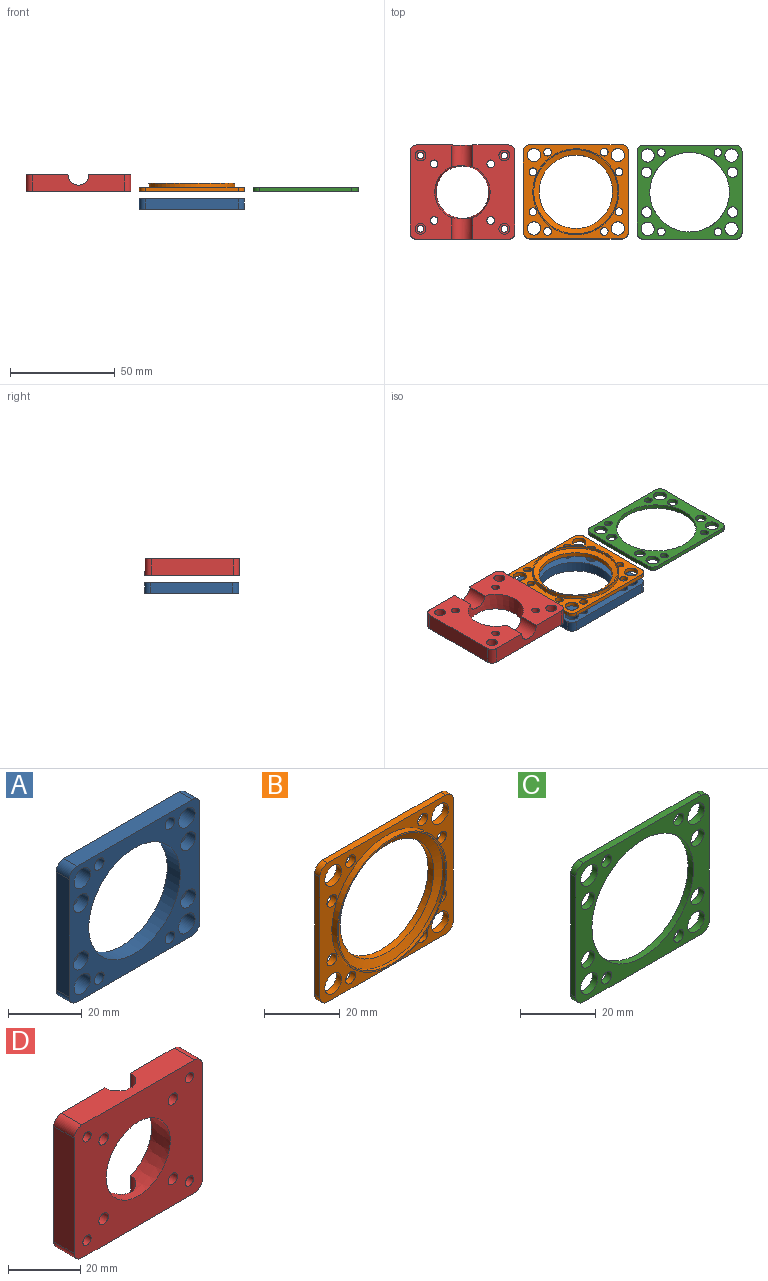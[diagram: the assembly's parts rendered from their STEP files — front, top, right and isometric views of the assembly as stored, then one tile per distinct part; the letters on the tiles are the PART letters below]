
ASSEMBLY  parts=4 mates=4
PART A: 31 faces, bbox 50x5x45 mm
  f0: plane 44x5mm, normal (0,0,1), area 220mm2, adj f4,f5,f27,f30
  f1: plane 39x5mm, normal (-1,0,0), area 195mm2, adj f4,f5,f27,f28
  f2: plane 44x5mm, normal (0,0,-1), area 220mm2, adj f4,f5,f28,f29
  f3: plane 39x5mm, normal (1,0,0), area 195mm2, adj f4,f5,f29,f30
  f4: plane 50x45mm, normal (0,-1,0), area 1010.4mm2, adj f0,f1,f2,f3,f6,f7,f8,f9
  f5: plane 50x45mm, normal (0,1,0), area 1069.5mm2, adj f0,f1,f2,f3,f6,f7,f8,f9
  f6: cylinder r=17.5mm len=35mm, axis (0,-1,0), area 549.8mm2, adj f4,f5
  f7: cylinder r=3.15mm len=6.3mm, axis (0,-1,0), area 99mm2, adj f4,f5
  f8: cylinder r=3.15mm len=6.3mm, axis (0,-1,0), area 99mm2, adj f4,f5
  f9: cylinder r=3.15mm len=6.3mm, axis (0,-1,0), area 99mm2, adj f4,f5
  f10: cylinder r=3.15mm len=6.3mm, axis (0,-1,0), area 99mm2, adj f4,f5
  f11: cylinder r=1.85mm len=3.7mm, axis (0,-1,0), area 17.4mm2, adj f5,f12
  f12: plane 5.7x5.7mm, normal (0,-1,0), area 14.8mm2, adj f11,f13
  f13: cylinder r=2.85mm len=5.7mm, axis (0,-1,0), area 62.7mm2, adj f4,f12
  f14: cylinder r=1.85mm len=3.7mm, axis (0,-1,0), area 17.4mm2, adj f5,f15
  f15: plane 5.7x5.7mm, normal (0,-1,0), area 14.8mm2, adj f14,f16
  f16: cylinder r=2.85mm len=5.7mm, axis (0,-1,0), area 62.7mm2, adj f4,f15
  f17: cylinder r=1.85mm len=3.7mm, axis (0,-1,0), area 17.4mm2, adj f5,f18
  f18: plane 5.7x5.7mm, normal (0,-1,0), area 14.8mm2, adj f17,f19
  f19: cylinder r=2.85mm len=5.7mm, axis (0,-1,0), area 62.7mm2, adj f4,f18
  f20: cylinder r=1.85mm len=3.7mm, axis (0,-1,0), area 17.4mm2, adj f5,f21
  f21: plane 5.7x5.7mm, normal (0,-1,0), area 14.8mm2, adj f20,f22
  f22: cylinder r=2.85mm len=5.7mm, axis (0,-1,0), area 62.7mm2, adj f4,f21
  f23: cylinder r=1.85mm len=5mm, axis (0,-1,0), area 58.1mm2, adj f4,f5
  f24: cylinder r=1.85mm len=5mm, axis (0,-1,0), area 58.1mm2, adj f4,f5
  f25: cylinder r=1.85mm len=5mm, axis (0,-1,0), area 58.1mm2, adj f4,f5
  f26: cylinder r=1.85mm len=5mm, axis (0,-1,0), area 58.1mm2, adj f4,f5
  f27: cylinder r=3mm len=5mm, axis (0,-1,0), area 23.6mm2, adj f0,f1,f4,f5
  f28: cylinder r=3mm len=5mm, axis (0,1,0), area 23.6mm2, adj f1,f2,f4,f5
  f29: cylinder r=3mm len=5mm, axis (0,-1,0), area 23.6mm2, adj f2,f3,f4,f5
  f30: cylinder r=3mm len=5mm, axis (0,1,0), area 23.6mm2, adj f0,f3,f4,f5
PART B: 27 faces, bbox 50x6.7x45 mm
  f0: plane 39x2mm, normal (-1,0,0), area 78mm2, adj f4,f5,f19,f22
  f1: plane 44x2mm, normal (0,0,-1), area 88mm2, adj f4,f5,f19,f20
  f2: plane 39x2mm, normal (1,0,0), area 78mm2, adj f4,f5,f20,f21
  f3: plane 44x2mm, normal (0,0,1), area 88mm2, adj f4,f5,f21,f22
  f4: plane 50x45mm, normal (0,-1,0), area 711.3mm2, adj f0,f1,f2,f3,f7,f8,f9,f10
  f5: plane 50x45mm, normal (0,1,0), area 1069.5mm2, adj f0,f1,f2,f3,f6,f7,f8,f9
  f6: cylinder r=17.5mm len=35mm, axis (0,-1,0), area 229.3mm2, adj f5,f25
  f7: cylinder r=3.15mm len=6.3mm, axis (0,-1,0), area 39.6mm2, adj f4,f5
  f8: cylinder r=3.15mm len=6.3mm, axis (0,-1,0), area 39.6mm2, adj f4,f5
  f9: cylinder r=3.15mm len=6.3mm, axis (0,-1,0), area 39.6mm2, adj f4,f5
  f10: cylinder r=3.15mm len=6.3mm, axis (0,-1,0), area 39.6mm2, adj f4,f5
  f11: cylinder r=1.85mm len=3.7mm, axis (0,-1,0), area 23.2mm2, adj f4,f5
  f12: cylinder r=1.85mm len=3.7mm, axis (0,-1,0), area 23.2mm2, adj f4,f5
  f13: cylinder r=1.85mm len=3.7mm, axis (0,-1,0), area 23.2mm2, adj f4,f5
  f14: cylinder r=1.85mm len=3.7mm, axis (0,-1,0), area 23.2mm2, adj f4,f5
  f15: cylinder r=1.85mm len=3.7mm, axis (0,-1,0), area 23.2mm2, adj f4,f5
  f16: cylinder r=1.85mm len=3.7mm, axis (0,-1,0), area 23.2mm2, adj f4,f5
  f17: cylinder r=1.85mm len=3.7mm, axis (0,-1,0), area 23.2mm2, adj f4,f5
  f18: cylinder r=1.85mm len=3.7mm, axis (0,-1,0), area 23.2mm2, adj f4,f5
  f19: cylinder r=3mm len=3mm, axis (0,-1,0), area 9.4mm2, adj f0,f1,f4,f5
  f20: cylinder r=3mm len=3mm, axis (0,1,0), area 9.4mm2, adj f1,f2,f4,f5
  f21: cylinder r=3mm len=3mm, axis (0,-1,0), area 9.4mm2, adj f2,f3,f4,f5
  f22: cylinder r=3mm len=3mm, axis (0,1,0), area 9.4mm2, adj f0,f3,f4,f5
  f23: cylinder r=20.5mm len=41mm, axis (0,1,0), area 257.6mm2, adj f4,f24
  f24: plane 41x41mm, normal (0,-1,0), area 51mm2, adj f23,f26
  f25: sphere r=60.95mm, area 323mm2, adj f6,f26
  f26: cylinder r=20.1mm len=40.2mm, axis (0,-1,0), area 135.3mm2, adj f24,f25
PART C: 23 faces, bbox 50x2x45 mm
  f0: plane 44x2mm, normal (0,0,1), area 88mm2, adj f4,f5,f19,f22
  f1: plane 39x2mm, normal (-1,0,0), area 78mm2, adj f4,f5,f19,f20
  f2: plane 44x2mm, normal (0,0,-1), area 88mm2, adj f4,f5,f20,f21
  f3: plane 39x2mm, normal (1,0,0), area 78mm2, adj f4,f5,f21,f22
  f4: plane 50x45mm, normal (0,-1,0), area 861.9mm2, adj f0,f1,f2,f3,f6,f7,f8,f9
  f5: plane 50x45mm, normal (0,1,0), area 861.9mm2, adj f0,f1,f2,f3,f6,f7,f8,f9
  f6: cylinder r=2.5mm len=5mm, axis (0,-1,0), area 31.4mm2, adj f4,f5
  f7: cylinder r=3.15mm len=6.3mm, axis (0,-1,0), area 39.6mm2, adj f4,f5
  f8: cylinder r=3.15mm len=6.3mm, axis (0,-1,0), area 39.6mm2, adj f4,f5
  f9: cylinder r=3.15mm len=6.3mm, axis (0,-1,0), area 39.6mm2, adj f4,f5
  f10: cylinder r=3.15mm len=6.3mm, axis (0,-1,0), area 39.6mm2, adj f4,f5
  f11: cylinder r=2.5mm len=5mm, axis (0,-1,0), area 31.4mm2, adj f4,f5
  f12: cylinder r=2.5mm len=5mm, axis (0,-1,0), area 31.4mm2, adj f4,f5
  f13: cylinder r=19mm len=38mm, axis (0,-1,0), area 238.8mm2, adj f4,f5
  f14: cylinder r=2.5mm len=5mm, axis (0,-1,0), area 31.4mm2, adj f4,f5
  f15: cylinder r=1.85mm len=3.7mm, axis (0,-1,0), area 23.2mm2, adj f4,f5
  f16: cylinder r=1.85mm len=3.7mm, axis (0,-1,0), area 23.2mm2, adj f4,f5
  f17: cylinder r=1.85mm len=3.7mm, axis (0,-1,0), area 23.2mm2, adj f4,f5
  f18: cylinder r=1.85mm len=3.7mm, axis (0,-1,0), area 23.2mm2, adj f4,f5
  f19: cylinder r=3mm len=3mm, axis (0,-1,0), area 9.4mm2, adj f0,f1,f4,f5
  f20: cylinder r=3mm len=3mm, axis (0,1,0), area 9.4mm2, adj f1,f2,f4,f5
  f21: cylinder r=3mm len=3mm, axis (0,-1,0), area 9.4mm2, adj f2,f3,f4,f5
  f22: cylinder r=3mm len=3mm, axis (0,1,0), area 9.4mm2, adj f0,f3,f4,f5
PART D: 30 faces, bbox 50x8x45 mm
  f0: plane 44x8mm, normal (0,0,1), area 312.7mm2, adj f1,f9,f10,f25,f27,f28
  f1: plane 45x20mm, normal (0,1,0), area 687.2mm2, adj f0,f6,f8,f11,f13,f15,f20,f23
  f2: cylinder r=1.6mm len=4.5mm, axis (0,-1,0), area 45.2mm2, adj f9,f18
  f3: cylinder r=1.6mm len=4.5mm, axis (0,-1,0), area 45.2mm2, adj f9,f16
  f4: cylinder r=1.6mm len=4.5mm, axis (0,-1,0), area 45.2mm2, adj f9,f14
  f5: cylinder r=1.6mm len=4.5mm, axis (0,-1,0), area 45.2mm2, adj f9,f12
  f6: plane 44x8mm, normal (0,0,-1), area 312.7mm2, adj f1,f9,f10,f24,f26,f29
  f7: plane 39x8mm, normal (1,0,0), area 312mm2, adj f9,f10,f26,f27
  f8: plane 39x8mm, normal (-1,0,0), area 312mm2, adj f1,f9,f28,f29
  f9: plane 50x45mm, normal (0,-1,0), area 1676.2mm2, adj f0,f2,f3,f4,f5,f6,f7,f8
  f10: plane 45x20mm, normal (0,1,0), area 687.2mm2, adj f0,f6,f7,f11,f17,f19,f21,f22
  f11: cone r=12.5mm half-angle=5deg, axis (0,1,0), area 568mm2, adj f1,f9,f10,f24,f25
  f12: plane 5.2x5.2mm, normal (0,1,0), area 13.2mm2, adj f5,f13
  f13: cylinder r=2.6mm len=5.2mm, axis (0,1,0), area 57.2mm2, adj f1,f12
  f14: plane 5.2x5.2mm, normal (0,1,0), area 13.2mm2, adj f4,f15
  f15: cylinder r=2.6mm len=5.2mm, axis (0,1,0), area 57.2mm2, adj f1,f14
  f16: plane 5.2x5.2mm, normal (0,1,0), area 13.2mm2, adj f3,f17
  f17: cylinder r=2.6mm len=5.2mm, axis (0,1,0), area 57.2mm2, adj f10,f16
  f18: plane 5.2x5.2mm, normal (0,1,0), area 13.2mm2, adj f2,f19
  f19: cylinder r=2.6mm len=5.2mm, axis (0,1,0), area 57.2mm2, adj f10,f18
  f20: cylinder r=1.85mm len=8mm, axis (0,-1,0), area 93mm2, adj f1,f9
  f21: cylinder r=1.85mm len=8mm, axis (0,-1,0), area 93mm2, adj f9,f10
  f22: cylinder r=1.85mm len=8mm, axis (0,-1,0), area 93mm2, adj f9,f10
  f23: cylinder r=1.85mm len=8mm, axis (0,-1,0), area 93mm2, adj f1,f9
  f24: cylinder r=5mm len=10.34mm, axis (0,0,1), area 158.2mm2, adj f1,f6,f10,f11
  f25: cylinder r=5mm len=10.34mm, axis (0,0,1), area 158.2mm2, adj f0,f1,f10,f11
  f26: cylinder r=3mm len=8mm, axis (0,1,0), area 37.7mm2, adj f6,f7,f9,f10
  f27: cylinder r=3mm len=8mm, axis (0,-1,0), area 37.7mm2, adj f0,f7,f9,f10
  f28: cylinder r=3mm len=8mm, axis (0,1,0), area 37.7mm2, adj f0,f1,f8,f9
  f29: cylinder r=3mm len=8mm, axis (0,-1,0), area 37.7mm2, adj f1,f6,f8,f9
PLACE A rot(axis=(-1,0,0),90deg) t=(54.1,0.2,-48.25)mm
PLACE B rot(axis=(-1,0,0),90deg) t=(54.1,0.2,-35)mm
PLACE C rot(axis=(-1,0,0),90deg) t=(108.3,0,-44.75)mm
PLACE D rot(axis=(1,0,0),90deg) t=(0,0,3)mm
MATE planar C.f13 <-> D.f11  axis (0,0,-1) through (108.3,0,0)mm
MATE parallel A.f0 <-> D.f6  axis (0,1,0) through (54.1,22.7,-6)mm
MATE planar D.f11 <-> B.f6  axis (0,0,-1) through (0,0,0)mm
MATE parallel A.f0 <-> C.f0  axis (0,1,0) through (54.1,22.7,-6)mm
